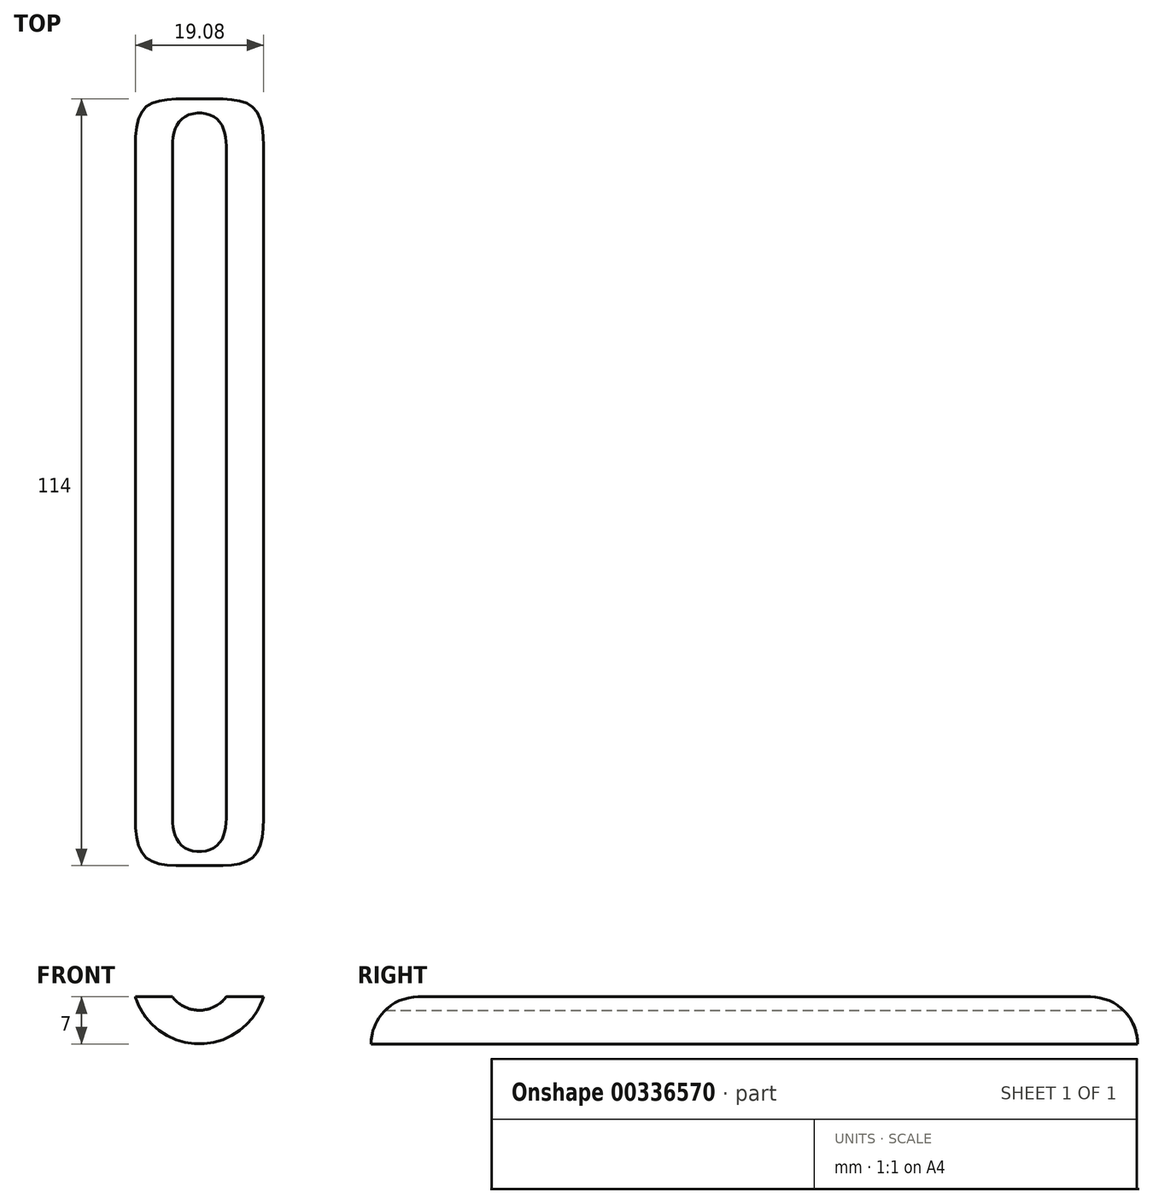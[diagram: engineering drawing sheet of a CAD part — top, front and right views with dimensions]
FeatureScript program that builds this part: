
annotation { "Feature Type Name" : "Feature", "Feature Type Description" : "" }
export const myFeature = defineFeature(function(context is Context, id is Id, definition is map)
    precondition{}
    {
        {
            var Q0;
            Q0=qCreatedBy(makeId("Front.planeOp"),FACE);
            var sketch = newSketch(context, id + "F0", { "sketchPlane" : qUnion([Q0])});
            skCircle(sketch, "E0", {"center": v(0, 0) * mm, "radius": 10 * mm});
            skCircle(sketch, "E1", {"center": v(0, 0) * mm, "radius": 5 * mm});
            skSolve(sketch);
        }
        {
            var Q0;
            Q0=qSketchRegion(id+"F0",true);
            extrude(context, id + "F1", {"entities" : qUnion([Q0]), "depth" : 180 * mm, "offsetDistance" : 25 * mm});
        }
        {
            var Q0;
            Q0=qCreatedBy(makeId("Right.planeOp"),FACE);
            var sketch = newSketch(context, id + "F2", { "sketchPlane" : qUnion([Q0])});
            skLineSegment(sketch, "E2.bottom", {"start": v(-140, -3) * mm, "end": v(-40, -3) * mm});
            skArc(sketch, "E3", {"start": v(-140, -3) * mm, "mid": v(-144.95, -5.05) * mm, "end": v(-147, -10) * mm});
            skArc(sketch, "E4", {"start": v(-33, -10) * mm, "mid": v(-35.05, -5.05) * mm, "end": v(-40, -3) * mm});
            skLineSegment(sketch, "E5", {"start": v(-147, -10) * mm, "end": v(-188.98, -10) * mm});
            skLineSegment(sketch, "E6", {"start": v(-188.98, -10) * mm, "end": v(-179.4, 25.04) * mm});
            skLineSegment(sketch, "E7", {"start": v(-179.4, 25.04) * mm, "end": v(19.1, 33.98) * mm});
            skLineSegment(sketch, "E8", {"start": v(19.1, 33.98) * mm, "end": v(36.5, -33.98) * mm});
            skLineSegment(sketch, "E9", {"start": v(36.5, -33.98) * mm, "end": v(-14.68, -24.97) * mm});
            skLineSegment(sketch, "E10", {"start": v(-14.68, -24.97) * mm, "end": v(-33, -10) * mm});
            skPoint(sketch, "E2.top.end.orphan", {"position": v(-40, -17) * mm});
            skPoint(sketch, "E2.top.start.orphan", {"position": v(-140, -17) * mm});
            skSolve(sketch);
        }
        {
            var Q0;
            Q0 = qSketchRegion(id + "F2", true);
            extrude(context, id + "F3", {"entities" : qUnion([Q0]), "operationType" : NewBodyOperationType.REMOVE, "endBound" : BoundingType.SYMMETRIC, "oppositeDirection" : true, "depth" : 40 * mm, "offsetDistance" : 25 * mm});
        }
    });
